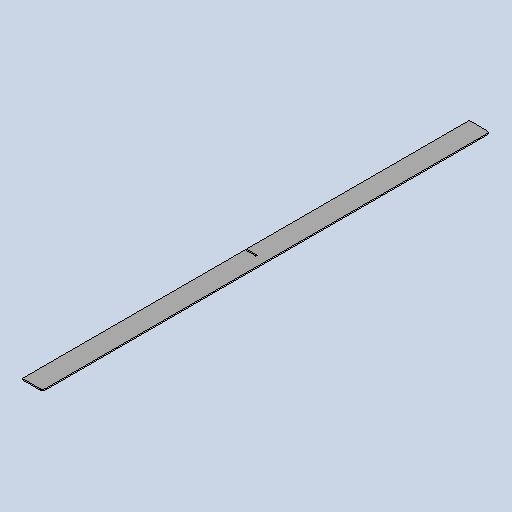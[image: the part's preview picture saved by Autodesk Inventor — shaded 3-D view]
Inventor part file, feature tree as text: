
AUTODESK INVENTOR PART (.ipt)
format: ipt  version: 2025 (Build 290162010, 162A)  size: 160,768 bytes
history: native  units: mm
features: sheet_metal_op x1, chamfer x1, sketch x1, other x1
ambient origin geometry x8: Origin, YZ Plane, XZ Plane, XY Plane, X Axis, Y Axis, Z Axis, Center Point
bodies: Body1 (feature_tree)
feature tree (4):
  sheet_metal_op  "Face2"
  chamfer  "Corner Round2"
  sketch  "Sketch1"  dims[d15=3.0mm d17=1098.0mm d18=50.0mm d19=3.0mm d20=26.0mm d22=6.0mm]
  other  "Plate2"
